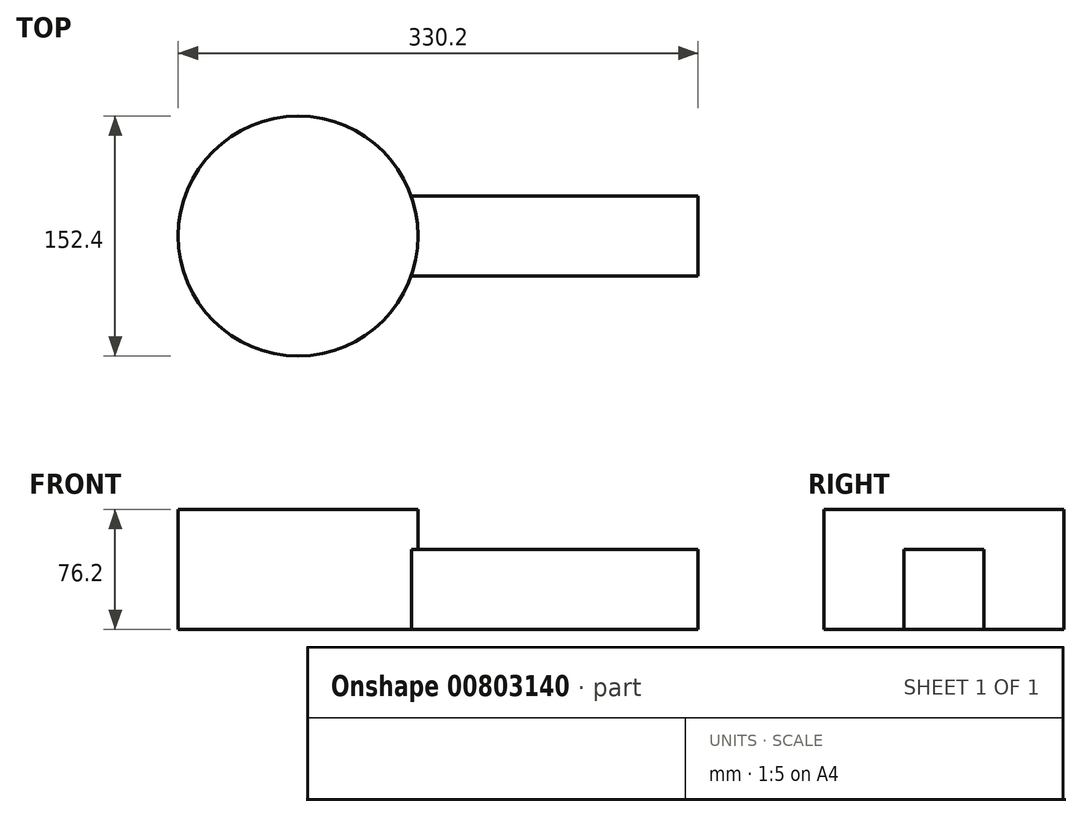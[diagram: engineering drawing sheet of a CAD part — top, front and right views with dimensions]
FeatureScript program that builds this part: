
annotation { "Feature Type Name" : "Feature", "Feature Type Description" : "" }
export const myFeature = defineFeature(function(context is Context, id is Id, definition is map)
    precondition{}
    {
        {
            var Q0;
            Q0=qCreatedBy(makeId("Front.planeOp"),FACE);
            var sketch = newSketch(context, id + "F0", { "sketchPlane" : qUnion([Q0])});
            skLineSegment(sketch, "E0", {"start": v(0, 0) * mm, "end": v(254, 0) * mm});
            skLineSegment(sketch, "E1", {"start": v(254, 0) * mm, "end": v(254, 50.8) * mm});
            skLineSegment(sketch, "E2", {"start": v(254, 50.8) * mm, "end": v(0, 50.8) * mm});
            skLineSegment(sketch, "E3", {"start": v(0, 50.8) * mm, "end": v(0, 0) * mm});
            skSolve(sketch);
        }
        {
            var Q0;
            Q0=makeQuery(id+"F0.imprint","IMPRINT",FACE,{"disambiguationData":[TD([[makeQuery(id+"F0.imprint","IMPRINT",EDGE,{"derivedFrom":sQuery(id+"F0.wireOp",EDGE,"E0")}),1.0]])]});
            extrude(context, id + "F1", {"entities" : qUnion([Q0]), "endBound" : BoundingType.SYMMETRIC, "depth" : 50.8 * mm, "offsetDistance" : 25.4 * mm});
        }
        {
            var Q0;
            Q0=qCreatedBy(makeId("Front.planeOp"),FACE);
            var sketch = newSketch(context, id + "F2", { "sketchPlane" : qUnion([Q0])});
            skLineSegment(sketch, "E4", {"start": v(0, 0) * mm, "end": v(0, 112.87) * mm});
            skSolve(sketch);
        }
        {
            var Q0;
            Q0=qCreatedBy(makeId("Front.planeOp"),FACE);
            var sketch = newSketch(context, id + "F3", { "sketchPlane" : qUnion([Q0])});
            skLineSegment(sketch, "E5", {"start": v(0, 0) * mm, "end": v(-76.2, 0) * mm});
            skLineSegment(sketch, "E6", {"start": v(-76.2, 0) * mm, "end": v(-76.2, 76.2) * mm});
            skLineSegment(sketch, "E7", {"start": v(-76.2, 76.2) * mm, "end": v(0, 76.2) * mm});
            skLineSegment(sketch, "E8", {"start": v(0, 76.2) * mm, "end": v(0, 0) * mm});
            skSolve(sketch);
        }
        {
            var Q0;
            Q0=makeQuery(id+"F3.imprint","IMPRINT",FACE,{"disambiguationData":[TD([[makeQuery(id+"F3.imprint","IMPRINT",EDGE,{"derivedFrom":sQuery(id+"F3.wireOp",EDGE,"E5")}),-1.0]])]});
            var Q1;
            Q1=sQuery(id+"F2.wireOp",EDGE,"E4");
            revolve(context, id + "F4", {"operationType" : NewBodyOperationType.ADD, "surfaceOperationType" : NewSurfaceOperationType.NEW, "entities" : qUnion([Q0]), "axis" : qUnion([Q1]), "revolveType" : RevolveType.FULL});
        }
    });
